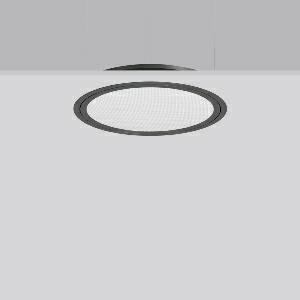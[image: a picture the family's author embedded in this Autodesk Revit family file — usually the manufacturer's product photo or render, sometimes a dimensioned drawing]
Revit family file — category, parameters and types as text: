
# Revit family: triona_round_e_312423_0031_12_dad3
name_source: partatom
category: Lighting Fixtures
units: mm (PartAtom-declared; Revit-internal decimal feet)

## family parameters
Cut with Voids When Loaded = No
Host = Face
Light Source = No
Part Type = Normal
Room Calculation Point = No
Round Connector Dimension = Use Diameter
Shared = No

## types (1)
- TRIONA round E (1 x LED Modul 830, 3150 lm, 3000)
    Apparent Load = 28 VA
    CIE Flux Codes = 58 87 97 100 100
    Color Rendering = 80
    Color Temperature = 3000
    Default Elevation = 1800 mm
    Description = Series: TRIONA round
Decorative round LED recessed surface luminaire. Cover made of sheet steel, powder-coated. Frame made of aluminium, powder-coated. Recessed ring: aluminium extrusion profile, powder coated. Light emission through a diffuser in plastic, opal/prismatic. Lightguide and diffuser made of non-yellowing plastic (PMMA). Lateral light emission (RZB SIDELITE technology) for above-average homogeneous light distribution. Suitable for installation in cavity ceilings. Tool-free mounting system thanks to the rocker arm mechanism (patent pending). Electronic ballast included. Very easy installation thanks to Plug+Play connection. 
Colour: anthracite metallic (DB703)
Diameter: 505 mm
Height: 2 mm
Cut-out diameter: 482 mm
Recess height: 100 mm
Luminaire: recess height: 89 mm
Lamp: LED
Socket: without socket
Colour temperature: 3000K
Colour rendering index (CRI): 80
System power: 28 W
Rated luminous flux: 3150 lm
Luminous efficiency: 113 lm/W
Control gear: Converter, dimmable, DALI
Protection class: I
Type of protection: IP 40
    Height = 0 mm  [stored 0 ft]
    Lamp = 1 x LED Modul 830
    Lamp Light Flux = 3150 lm
    Lamp count = 1
    Length = 505 mm
    Lifetime = 50000 h
    Luminous efficacy = 113 lm/W
    Manufacturer = RZB
    ModVariant = No
    Model = 312423.0031.12
    Mounting Place = Ceiling
    Mounting Type = Recessed
    Number of Poles = 1
    OnlyDefault = Yes
    Power Factor = 1
    Product Name = TRIONA round E
    Product group = Recessed modular luminaires
    ProductGroupID = 406
    Protection Class = Protection class I
    Protection Degree = IP 20
    RLX_Detail_Level = 1
    RLX_Emergency_Light_Flux = 0 lm
    RLX_Emergency_Type = 0
    RLX_Emergency_Type_DB = No
    RlxData = <blob elided: 34929 chars, md5=284562b5>
    Socket = socket
    Standby Power = 0 W
    System Light Flux = 3150 lm
    System Power = 28 W
    Type Comments = Product without accessories
    Type Image = 312423.0031.12.jpg
    URL = http://relux.com
    VarID = ---
    Voltage = 230 V
    Voltage Range = 220-240 V
    Weight = 0.00 kg
    Width = 0 mm  [stored 0 ft]

note: [stored X ft] marks values corroborated as IEEE doubles in the binary element streams (Revit-internal decimal feet)

## geometry (parser evidence)
native form markers: Blend x4, Sweep x9
no freeform markers — native parametric forms only
